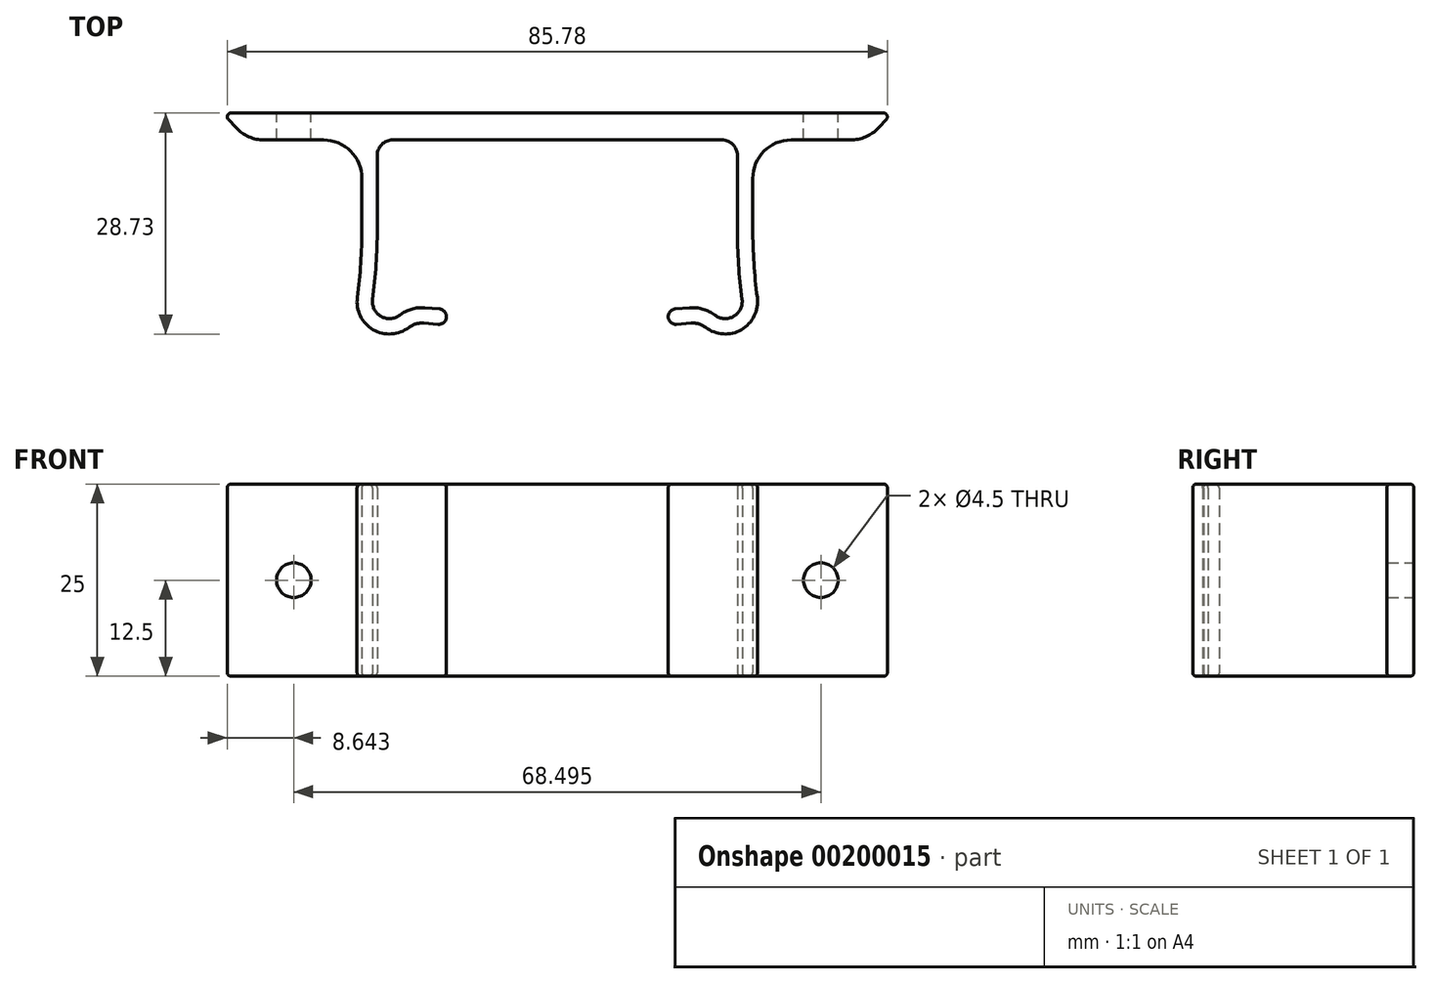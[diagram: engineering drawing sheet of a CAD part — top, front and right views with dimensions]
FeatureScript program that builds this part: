
annotation { "Feature Type Name" : "Feature", "Feature Type Description" : "" }
export const myFeature = defineFeature(function(context is Context, id is Id, definition is map)
    precondition{}
    {
        {
            var Q0;
            Q0=qCreatedBy(makeId("Top.planeOp"),FACE);
            var sketch = newSketch(context, id + "F0", { "sketchPlane" : qUnion([Q0])});
            skLineSegment(sketch, "E0.bottom", {"start": v(23, -11) * mm, "end": v(-23, -11) * mm, "construction": true});
            skLineSegment(sketch, "E0.top", {"start": v(23, 11) * mm, "end": v(-23, 11) * mm, "construction": true});
            skLineSegment(sketch, "E0.left", {"start": v(23, -11) * mm, "end": v(23, 11) * mm, "construction": true});
            skLineSegment(sketch, "E0.right", {"start": v(-23, -11) * mm, "end": v(-23, 11) * mm, "construction": true});
            skPoint(sketch, "E0.middle", {"position": v(0, 0) * mm});
            skLineSegment(sketch, "E1", {"start": v(0, 14.5) * mm, "end": v(0, -14.5) * mm, "construction": true});
            skPoint(sketch, "E1.startSnap0", {"position": v(0, 11) * mm});
            skLineSegment(sketch, "E2", {"start": v(-43.54, 14.5) * mm, "end": v(0, 14.5) * mm});
            skLineSegment(sketch, "E3", {"start": v(-40.26, 11) * mm, "end": v(-25.4, 11) * mm});
            skLineSegment(sketch, "E4", {"start": v(-23.4, 11) * mm, "end": v(-23.4, -0.58) * mm});
            skArc(sketch, "E5", {"start": v(-23.4, -0.58) * mm, "mid": v(-23.55, -5.16) * mm, "end": v(-24, -9.73) * mm});
            skArc(sketch, "E6", {"start": v(-24, -9.73) * mm, "mid": v(-22.93, -11.93) * mm, "end": v(-20.48, -11.78) * mm});
            skArc(sketch, "E7", {"start": v(-20.48, -11.78) * mm, "mid": v(-18.93, -11) * mm, "end": v(-17.2, -10.82) * mm});
            skArc(sketch, "E8.0", {"start": v(-19.27, -13.37) * mm, "mid": v(-18.37, -12.91) * mm, "end": v(-17.36, -12.8) * mm});
            skArc(sketch, "E8.1", {"start": v(-25.99, -9.46) * mm, "mid": v(-23.93, -13.66) * mm, "end": v(-19.27, -13.37) * mm});
            skArc(sketch, "E8.2", {"start": v(-25.4, -0.58) * mm, "mid": v(-25.55, -5.03) * mm, "end": v(-25.99, -9.46) * mm});
            skLineSegment(sketch, "E8.3", {"start": v(-25.4, 11) * mm, "end": v(-25.4, -0.58) * mm});
            skLineSegment(sketch, "E9", {"start": v(-17.59, -10.8) * mm, "end": v(-3.72, -10.8) * mm, "construction": true});
            skLineSegment(sketch, "E10.trimOffspring", {"start": v(-23.4, 11) * mm, "end": v(0, 11) * mm});
            skLineSegment(sketch, "E11", {"start": v(-43.54, 14.5) * mm, "end": v(-40.26, 11) * mm});
            skLineSegment(sketch, "E12.MirrorCS", {"start": v(23.4, 11) * mm, "end": v(0, 11) * mm});
            skArc(sketch, "E13.MirrorCS", {"start": v(19.27, -13.37) * mm, "mid": v(18.37, -12.91) * mm, "end": v(17.36, -12.8) * mm});
            skArc(sketch, "E14.MirrorCS", {"start": v(20.48, -11.78) * mm, "mid": v(18.93, -11) * mm, "end": v(17.2, -10.82) * mm});
            skArc(sketch, "E15.MirrorCS", {"start": v(24, -9.73) * mm, "mid": v(22.93, -11.93) * mm, "end": v(20.48, -11.78) * mm});
            skArc(sketch, "E16.MirrorCS", {"start": v(25.99, -9.46) * mm, "mid": v(23.93, -13.66) * mm, "end": v(19.27, -13.37) * mm});
            skArc(sketch, "E17.MirrorCS", {"start": v(23.4, -0.58) * mm, "mid": v(23.55, -5.16) * mm, "end": v(24, -9.73) * mm});
            skArc(sketch, "E18.MirrorCS", {"start": v(25.4, -0.58) * mm, "mid": v(25.55, -5.03) * mm, "end": v(25.99, -9.46) * mm});
            skLineSegment(sketch, "E19.MirrorCS", {"start": v(23.4, 11) * mm, "end": v(23.4, -0.58) * mm});
            skLineSegment(sketch, "E20.MirrorCS", {"start": v(25.4, 11) * mm, "end": v(25.4, -0.58) * mm});
            skLineSegment(sketch, "E21.MirrorCS", {"start": v(40.26, 11) * mm, "end": v(25.4, 11) * mm});
            skLineSegment(sketch, "E22.MirrorCS", {"start": v(43.54, 14.5) * mm, "end": v(0, 14.5) * mm});
            skLineSegment(sketch, "E23.MirrorCS", {"start": v(43.54, 14.5) * mm, "end": v(40.26, 11) * mm});
            skLineSegment(sketch, "E24", {"start": v(-17.36, -12.8) * mm, "end": v(-15.5, -12.96) * mm});
            skLineSegment(sketch, "E25", {"start": v(-17.2, -10.82) * mm, "end": v(-15.33, -10.97) * mm});
            skArc(sketch, "E26", {"start": v(-15.5, -12.96) * mm, "mid": v(-14.41, -12.04) * mm, "end": v(-15.33, -10.97) * mm});
            skArc(sketch, "E27.MirrorCS", {"start": v(15.5, -12.96) * mm, "mid": v(14.41, -12.04) * mm, "end": v(15.33, -10.97) * mm});
            skLineSegment(sketch, "E28.MirrorCS", {"start": v(17.36, -12.8) * mm, "end": v(15.5, -12.96) * mm});
            skLineSegment(sketch, "E29.MirrorCS", {"start": v(17.2, -10.82) * mm, "end": v(15.33, -10.97) * mm});
            skSolve(sketch);
        }
        {
            var Q0;
            Q0 = qSketchRegion(id + "F0", true);
            extrude(context, id + "F1", {"entities" : qUnion([Q0]), "depth" : 25 * mm});
        }
        {
            var Q0;
            Q0=makeQuery(id+"F1.opExtrude","SWEPT_EDGE",EDGE,{"disambiguationData":[OSD([sQuery(id+"F0.wireOp",EDGE,"E3"),sQuery(id+"F0.wireOp",EDGE,"E8.3")])]});
            var Q1;
            Q1=makeQuery(id+"F1.opExtrude","SWEPT_EDGE",EDGE,{"disambiguationData":[OSD([sQuery(id+"F0.wireOp",EDGE,"E20.MirrorCS"),sQuery(id+"F0.wireOp",EDGE,"E21.MirrorCS")])]});
            fillet(context, id + "F2", {"entities" : qUnion([Q0, Q1]), "radius" : 5 * mm, "tangentPropagation" : true, "allowEdgeOverflow" : false});
        }
        {
            var Q0;
            Q0=makeQuery(id+"F1.opExtrude","SWEPT_EDGE",EDGE,{"disambiguationData":[OSD([sQuery(id+"F0.wireOp",EDGE,"E12.MirrorCS"),sQuery(id+"F0.wireOp",EDGE,"E19.MirrorCS")])]});
            var Q1;
            Q1=makeQuery(id+"F1.opExtrude","SWEPT_EDGE",EDGE,{"disambiguationData":[OSD([sQuery(id+"F0.wireOp",EDGE,"E4"),sQuery(id+"F0.wireOp",EDGE,"E10.trimOffspring")])]});
            fillet(context, id + "F3", {"entities" : qUnion([Q0, Q1]), "radius" : 2 * mm, "tangentPropagation" : true, "allowEdgeOverflow" : false});
        }
        {
            var Q0;
            Q0=makeQuery(id+"F1.opExtrude","SWEPT_EDGE",EDGE,{"disambiguationData":[OSD([sQuery(id+"F0.wireOp",EDGE,"E3"),sQuery(id+"F0.wireOp",EDGE,"E11")])]});
            var Q1;
            Q1=makeQuery(id+"F1.opExtrude","SWEPT_EDGE",EDGE,{"disambiguationData":[OSD([sQuery(id+"F0.wireOp",EDGE,"E21.MirrorCS"),sQuery(id+"F0.wireOp",EDGE,"E23.MirrorCS")])]});
            fillet(context, id + "F4", {"entities" : qUnion([Q0, Q1]), "radius" : 5 * mm, "tangentPropagation" : true, "allowEdgeOverflow" : false});
        }
        {
            var Q0;
            Q0=makeQuery(id+"F1.opExtrude","SWEPT_EDGE",EDGE,{"disambiguationData":[OSD([sQuery(id+"F0.wireOp",EDGE,"E2"),sQuery(id+"F0.wireOp",EDGE,"E11")])]});
            var Q1;
            Q1=makeQuery(id+"F1.opExtrude","SWEPT_EDGE",EDGE,{"disambiguationData":[OSD([sQuery(id+"F0.wireOp",EDGE,"E22.MirrorCS"),sQuery(id+"F0.wireOp",EDGE,"E23.MirrorCS")])]});
            fillet(context, id + "F5", {"entities" : qUnion([Q0, Q1]), "radius" : 0.5 * mm, "tangentPropagation" : true, "allowEdgeOverflow" : false});
        }
        {
            var Q0;
            Q0=makeQuery(id+"F1.opExtrude","SWEPT_FACE",FACE,{"disambiguationData":[OSD([sQuery(id+"F0.wireOp",EDGE,"E2"),sQuery(id+"F0.wireOp",EDGE,"E22.MirrorCS")])]});
            var sketch = newSketch(context, id + "F6", { "sketchPlane" : qUnion([Q0])});
            skLineSegment(sketch, "E30", {"start": v(0, 25) * mm, "end": v(0, 0) * mm, "construction": true});
            skCircle(sketch, "E31", {"center": v(-34.25, 12.5) * mm, "radius": 2.25 * mm});
            skCircle(sketch, "E32", {"center": v(34.25, 12.5) * mm, "radius": 2.25 * mm});
            skLineSegment(sketch, "E33", {"start": v(-34.25, 12.5) * mm, "end": v(0, 12.5) * mm, "construction": true});
            skLineSegment(sketch, "E34", {"start": v(0, 12.5) * mm, "end": v(34.25, 12.5) * mm, "construction": true});
            skLineSegment(sketch, "E35", {"start": v(38.1, 19.07) * mm, "end": v(30.4, 19.07) * mm, "construction": true});
            skLineSegment(sketch, "E36", {"start": v(34.25, 19.07) * mm, "end": v(34.25, 12.5) * mm, "construction": true});
            skSolve(sketch);
        }
        {
            var Q0;
            Q0 = qSketchRegion(id + "F6", true);
            extrude(context, id + "F7", {"entities" : qUnion([Q0]), "operationType" : NewBodyOperationType.REMOVE, "endBound" : BoundingType.THROUGH_ALL, "oppositeDirection" : true, "depth" : 25 * mm});
        }
        {
            var Q0;
            Q0=makeQuery(id+"F1.opExtrude","CAP_EDGE",EDGE,{"disambiguationData":[OSD([sQuery(id+"F0.wireOp",EDGE,"E8.2")])],"isStart":true});
            var Q1;
            Q1=makeQuery(id+"F1.opExtrude","CAP_EDGE",EDGE,{"disambiguationData":[OSD([sQuery(id+"F0.wireOp",EDGE,"E8.3")])],"isStart":false});
            fillet(context, id + "F8", {"entities" : qUnion([Q0, Q1]), "radius" : 0.5 * mm, "tangentPropagation" : true, "allowEdgeOverflow" : false});
        }
    });
